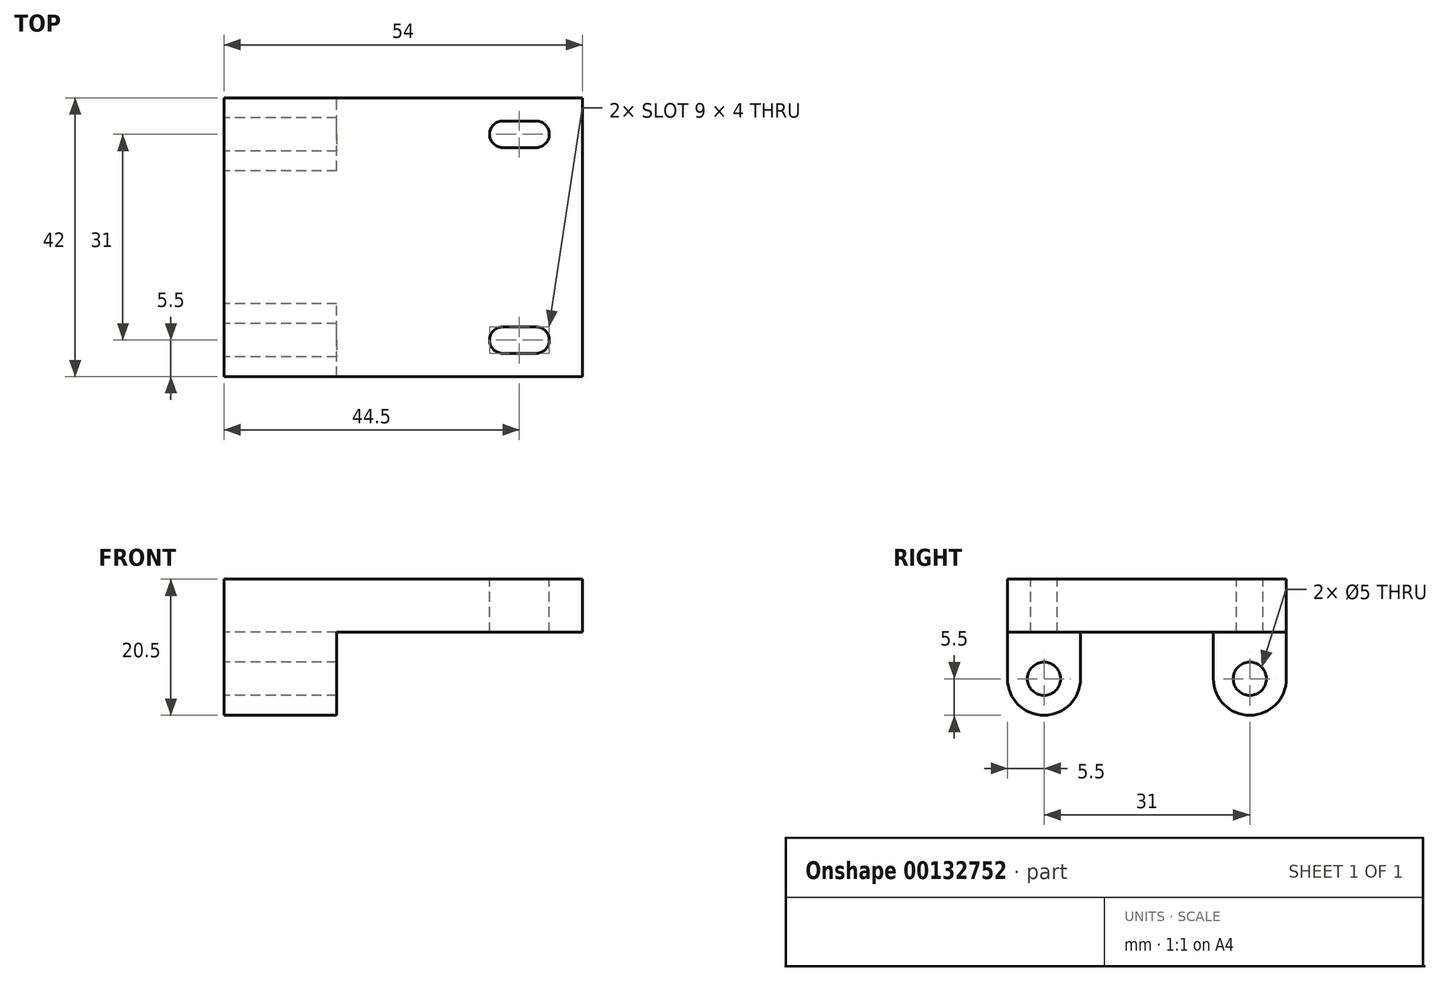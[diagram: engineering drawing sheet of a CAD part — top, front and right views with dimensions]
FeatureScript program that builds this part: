
annotation { "Feature Type Name" : "Feature", "Feature Type Description" : "" }
export const myFeature = defineFeature(function(context is Context, id is Id, definition is map)
    precondition{}
    {
        {
            var Q0;
            Q0=qCreatedBy(makeId("Front.planeOp"),FACE);
            var sketch = newSketch(context, id + "F0", { "sketchPlane" : qUnion([Q0])});
            skLineSegment(sketch, "E0", {"start": v(0, 0) * mm, "end": v(0, 22) * mm});
            skLineSegment(sketch, "E1", {"start": v(0, 22) * mm, "end": v(54, 22) * mm});
            skLineSegment(sketch, "E2", {"start": v(54, 22) * mm, "end": v(54, 14) * mm});
            skLineSegment(sketch, "E3", {"start": v(54, 14) * mm, "end": v(8, 14) * mm});
            skLineSegment(sketch, "E4", {"start": v(8, 14) * mm, "end": v(8, 0) * mm});
            skLineSegment(sketch, "E5", {"start": v(8, 0) * mm, "end": v(0, 0) * mm});
            skSolve(sketch);
        }
        {
            var Q0;
            Q0 = qSketchRegion(id + "F0", true);
            extrude(context, id + "F1", {"entities" : qUnion([Q0]), "depth" : 42 * mm});
        }
        {
            var Q0;
            Q0=makeQuery(id+"F1.opExtrude","SWEPT_FACE",FACE,{"disambiguationData":[OSD([sQuery(id+"F0.wireOp",EDGE,"E0")])]});
            var sketch = newSketch(context, id + "F2", { "sketchPlane" : qUnion([Q0])});
            skLineSegment(sketch, "E6", {"start": v(0, 7) * mm, "end": v(42, 7) * mm, "construction": true});
            skCircle(sketch, "E7", {"center": v(5.5, 7) * mm, "radius": 2.5 * mm});
            skCircle(sketch, "E8", {"center": v(36.5, 7) * mm, "radius": 2.5 * mm});
            skLineSegment(sketch, "E9.0", {"start": v(42, 14) * mm, "end": v(0, 14) * mm, "construction": true});
            skLineSegment(sketch, "E10", {"start": v(11, 7) * mm, "end": v(11, 14) * mm});
            skLineSegment(sketch, "E11", {"start": v(11, 14) * mm, "end": v(31, 14) * mm});
            skLineSegment(sketch, "E12", {"start": v(31, 14) * mm, "end": v(31, 7) * mm});
            skLineSegment(sketch, "E13", {"start": v(0, 7) * mm, "end": v(-13.12, 7) * mm});
            skLineSegment(sketch, "E14", {"start": v(-13.12, 7) * mm, "end": v(-13.12, -10.9) * mm});
            skLineSegment(sketch, "E15", {"start": v(-13.12, -10.9) * mm, "end": v(59.94, -10.9) * mm});
            skLineSegment(sketch, "E16", {"start": v(59.94, -10.9) * mm, "end": v(59.94, 7) * mm});
            skLineSegment(sketch, "E17", {"start": v(59.94, 7) * mm, "end": v(42, 7) * mm});
            skArc(sketch, "E18", {"start": v(0, 7) * mm, "mid": v(5.5, 1.5) * mm, "end": v(11, 7) * mm});
            skArc(sketch, "E19", {"start": v(31, 7) * mm, "mid": v(36.5, 1.5) * mm, "end": v(42, 7) * mm});
            skSolve(sketch);
        }
        {
            var Q0;
            Q0 = qSketchRegion(id + "F2", true);
            var Q1;
            Q1=makeQuery(id+"F1.opExtrude","SWEPT_FACE",FACE,{"disambiguationData":[OSD([sQuery(id+"F0.wireOp",EDGE,"E4")])]});
            extrude(context, id + "F3", {"entities" : qUnion([Q0]), "operationType" : NewBodyOperationType.REMOVE, "endBound" : BoundingType.UP_TO_SURFACE, "oppositeDirection" : true, "endBoundEntityFace" : qUnion([Q1]), "depth" : 25 * mm});
        }
        {
            var Q0;
            {var subQ1=sQuery(id+"F0.wireOp",EDGE,"E4");Q0=makeQuery(id+"F3.boolean.opBoolean","SPLIT",FACE,{"disambiguationData":[TD([makeQuery(id+"F3.opExtrude","SWEPT_FACE",FACE,{"disambiguationData":[OSD([sQuery(id+"F2.wireOp",EDGE,"E8")])]})])],"derivedFrom":makeQuery(id+"F1.opExtrude","SWEPT_FACE",FACE,{"disambiguationData":[OSD([subQ1])]})});}
            var sketch = newSketch(context, id + "F4", { "sketchPlane" : qUnion([Q0])});
            skLineSegment(sketch, "E20.0", {"start": v(-42, 14) * mm, "end": v(-31, 14) * mm});
            skLineSegment(sketch, "E20.1", {"start": v(-42, 14) * mm, "end": v(-42, 7) * mm});
            skArc(sketch, "E20.2", {"start": v(-31, 7) * mm, "mid": v(-36.5, 1.5) * mm, "end": v(-42, 7) * mm});
            skLineSegment(sketch, "E20.3", {"start": v(-31, 14) * mm, "end": v(-31, 7) * mm});
            skLineSegment(sketch, "E20.4", {"start": v(-11, 14) * mm, "end": v(0, 14) * mm});
            skLineSegment(sketch, "E20.5", {"start": v(-11, 7) * mm, "end": v(-11, 14) * mm});
            skArc(sketch, "E20.6", {"start": v(0, 7) * mm, "mid": v(-5.5, 1.5) * mm, "end": v(-11, 7) * mm});
            skLineSegment(sketch, "E20.7", {"start": v(0, 14) * mm, "end": v(0, 7) * mm});
            skCircle(sketch, "E21.0", {"center": v(-36.5, 7) * mm, "radius": 2.5 * mm});
            skCircle(sketch, "E21.1", {"center": v(-5.5, 7) * mm, "radius": 2.5 * mm});
            skSolve(sketch);
        }
        {
            var Q0;
            Q0 = qSketchRegion(id + "F4", true);
            extrude(context, id + "F5", {"entities" : qUnion([Q0]), "operationType" : NewBodyOperationType.ADD, "depth" : 9 * mm});
        }
        {
            var Q0;
            Q0=makeQuery(id+"F1.opExtrude","SWEPT_FACE",FACE,{"disambiguationData":[OSD([sQuery(id+"F0.wireOp",EDGE,"E1")])]});
            var sketch = newSketch(context, id + "F6", { "sketchPlane" : qUnion([Q0])});
            skLineSegment(sketch, "E22", {"start": v(47, 0) * mm, "end": v(47, -42) * mm, "construction": true});
            skArc(sketch, "E23", {"start": v(47, -7.5) * mm, "mid": v(49, -5.5) * mm, "end": v(47, -3.5) * mm});
            skArc(sketch, "E24", {"start": v(47, -38.5) * mm, "mid": v(49, -36.5) * mm, "end": v(47, -34.5) * mm});
            skLineSegment(sketch, "E25", {"start": v(47, -5.5) * mm, "end": v(0, -21) * mm, "construction": true});
            skLineSegment(sketch, "E26", {"start": v(0, -21) * mm, "end": v(47, -36.5) * mm, "construction": true});
            skLineSegment(sketch, "E27", {"start": v(47, -5.5) * mm, "end": v(42, -5.5) * mm, "construction": true});
            skLineSegment(sketch, "E28", {"start": v(47, -36.5) * mm, "end": v(42, -36.5) * mm, "construction": true});
            skArc(sketch, "E29", {"start": v(42, -3.5) * mm, "mid": v(40, -5.5) * mm, "end": v(42, -7.5) * mm});
            skArc(sketch, "E30", {"start": v(42, -34.5) * mm, "mid": v(40, -36.5) * mm, "end": v(42, -38.5) * mm});
            skLineSegment(sketch, "E31", {"start": v(42, -5.5) * mm, "end": v(42, -36.5) * mm, "construction": true});
            skLineSegment(sketch, "E32", {"start": v(42, -7.5) * mm, "end": v(47, -7.5) * mm});
            skLineSegment(sketch, "E33", {"start": v(47, -3.5) * mm, "end": v(42, -3.5) * mm});
            skLineSegment(sketch, "E34", {"start": v(42, -34.5) * mm, "end": v(47, -34.5) * mm});
            skLineSegment(sketch, "E35", {"start": v(47, -38.5) * mm, "end": v(42, -38.5) * mm});
            skSolve(sketch);
        }
        {
            var Q0;
            Q0 = qSketchRegion(id + "F6", true);
            var Q1;
            Q1=makeQuery(id+"F3.boolean.opBoolean","MERGE",FACE,{"derivedFrom":[makeQuery(id+"F1.opExtrude","SWEPT_FACE",FACE,{"disambiguationData":[OSD([sQuery(id+"F0.wireOp",EDGE,"E3")])]}),makeQuery(id+"F3.opExtrude","SWEPT_FACE",FACE,{"disambiguationData":[OSD([sQuery(id+"F2.wireOp",EDGE,"E11")])]})]});
            extrude(context, id + "F7", {"entities" : qUnion([Q0]), "operationType" : NewBodyOperationType.REMOVE, "endBound" : BoundingType.UP_TO_SURFACE, "oppositeDirection" : true, "endBoundEntityFace" : qUnion([Q1]), "depth" : 25 * mm});
        }
    });
